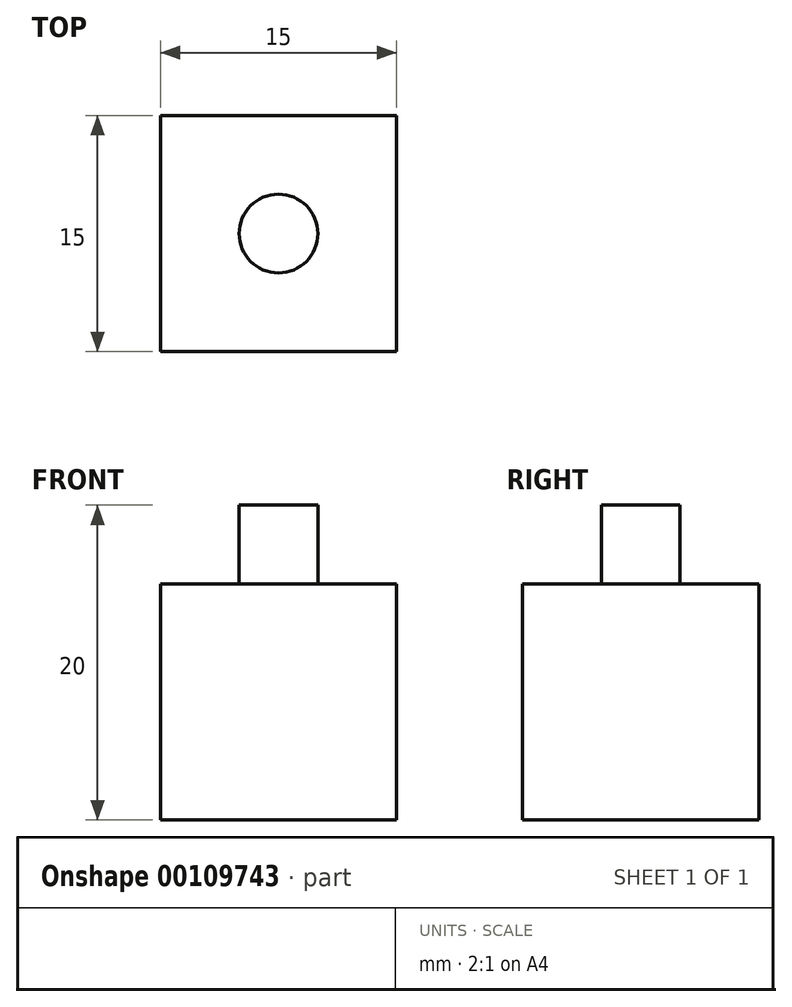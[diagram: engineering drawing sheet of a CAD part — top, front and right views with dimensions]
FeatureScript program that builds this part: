
annotation { "Feature Type Name" : "Feature", "Feature Type Description" : "" }
export const myFeature = defineFeature(function(context is Context, id is Id, definition is map)
    precondition{}
    {
        {
            var Q0;
            Q0=qCreatedBy(makeId("Top.planeOp"),FACE);
            var sketch = newSketch(context, id + "F0", { "sketchPlane" : qUnion([Q0])});
            skLineSegment(sketch, "E0.bottom", {"start": v(7.5, -7.5) * mm, "end": v(-7.5, -7.5) * mm});
            skLineSegment(sketch, "E0.top", {"start": v(7.5, 7.5) * mm, "end": v(-7.5, 7.5) * mm});
            skLineSegment(sketch, "E0.left", {"start": v(7.5, -7.5) * mm, "end": v(7.5, 7.5) * mm});
            skLineSegment(sketch, "E0.right", {"start": v(-7.5, -7.5) * mm, "end": v(-7.5, 7.5) * mm});
            skPoint(sketch, "E0.middle", {"position": v(0, 0) * mm});
            skSolve(sketch);
        }
        {
            var Q0;
            Q0=makeQuery(id+"F0.imprint","IMPRINT",FACE,{"disambiguationData":[TD([[makeQuery(id+"F0.imprint","IMPRINT",EDGE,{"derivedFrom":sQuery(id+"F0.wireOp",EDGE,"E0.bottom")}),-1.0]])]});
            extrude(context, id + "F1", {"entities" : qUnion([Q0]), "depth" : 15 * mm});
        }
        {
            var Q0;
            Q0=makeQuery(id+"F1.opExtrude","CAP_FACE",FACE,{"disambiguationData":[OSD([sQuery(id+"F0.wireOp",EDGE,"E0.bottom"),sQuery(id+"F0.wireOp",EDGE,"E0.top"),sQuery(id+"F0.wireOp",EDGE,"E0.left"),sQuery(id+"F0.wireOp",EDGE,"E0.right")])],"isStart":false});
            var sketch = newSketch(context, id + "F2", { "sketchPlane" : qUnion([Q0])});
            skCircle(sketch, "E1", {"center": v(0, 0) * mm, "radius": 2.5 * mm});
            skSolve(sketch);
        }
        {
            var Q0;
            Q0=makeQuery(id+"F2.imprint","IMPRINT",FACE,{"disambiguationData":[TD([[makeQuery(id+"F2.imprint","IMPRINT",EDGE,{"derivedFrom":sQuery(id+"F2.wireOp",EDGE,"E1")}),1.0]])]});
            extrude(context, id + "F3", {"entities" : qUnion([Q0]), "operationType" : NewBodyOperationType.ADD, "depth" : 5 * mm});
        }
    });
